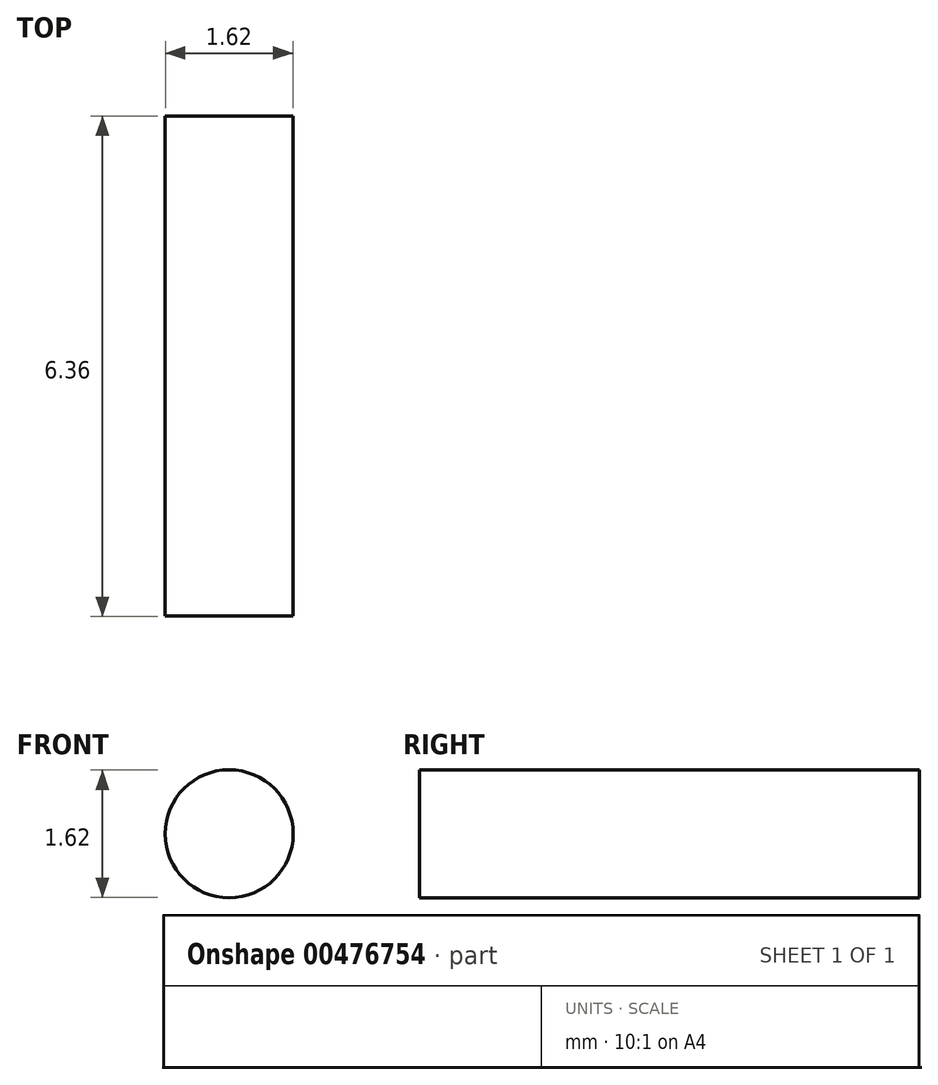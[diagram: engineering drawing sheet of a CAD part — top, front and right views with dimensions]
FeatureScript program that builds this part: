
annotation { "Feature Type Name" : "Feature", "Feature Type Description" : "" }
export const myFeature = defineFeature(function(context is Context, id is Id, definition is map)
    precondition{}
    {
        {
            var Q0;
            Q0=qCreatedBy(makeId("Front.planeOp"),FACE);
            var sketch = newSketch(context, id + "F0", { "sketchPlane" : qUnion([Q0])});
            skCircle(sketch, "E0", {"center": v(0, 0) * mm, "radius": 0.81 * mm});
            skSolve(sketch);
        }
        {
            var Q0;
            Q0=makeQuery(id+"F0.imprint","IMPRINT",FACE,{"disambiguationData":[TD([[makeQuery(id+"F0.imprint","IMPRINT",EDGE,{"derivedFrom":sQuery(id+"F0.wireOp",EDGE,"E0")}),1.0]])]});
            extrude(context, id + "F1", {"entities" : qUnion([Q0]), "depth" : 6.35 * mm, "symmetric" : true});
        }
    });
